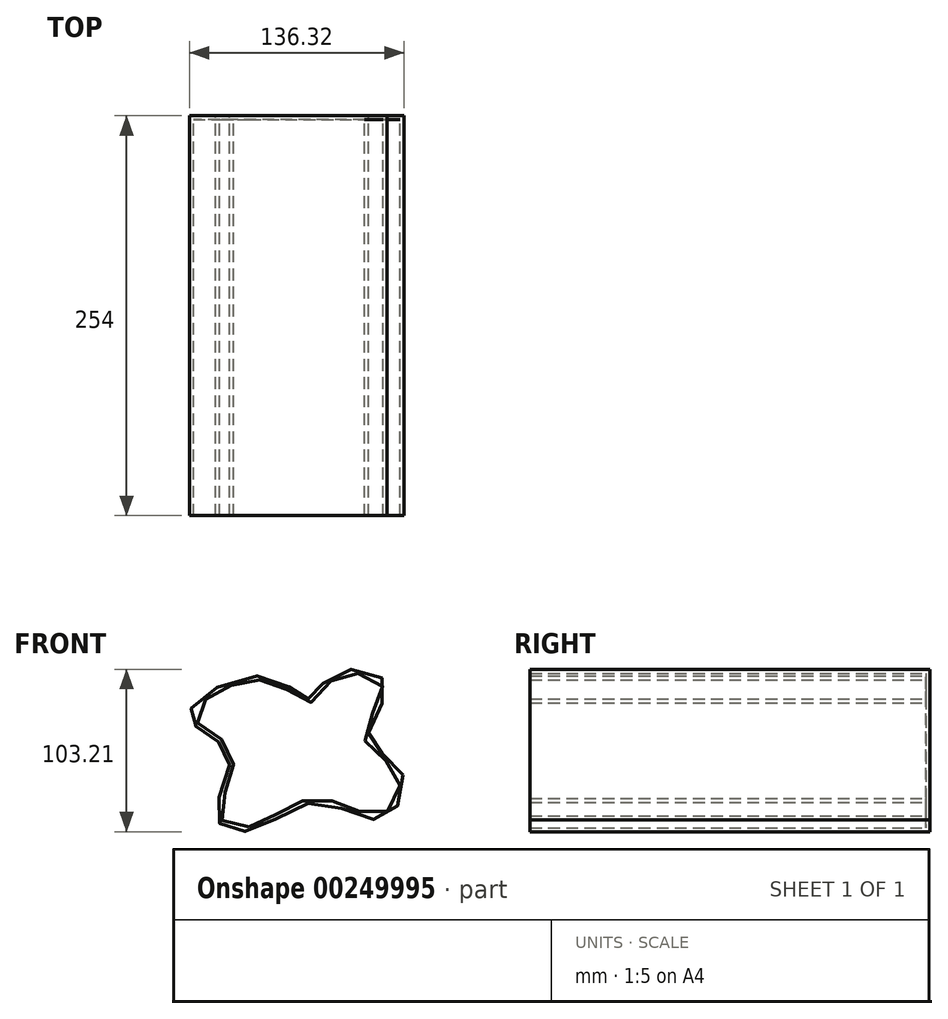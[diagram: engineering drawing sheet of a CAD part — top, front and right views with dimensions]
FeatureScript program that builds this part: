
annotation { "Feature Type Name" : "Feature", "Feature Type Description" : "" }
export const myFeature = defineFeature(function(context is Context, id is Id, definition is map)
    precondition{}
    {
        {
            var Q0;
            Q0=qCreatedBy(makeId("Front.planeOp"),FACE);
            var sketch = newSketch(context, id + "F0", { "sketchPlane" : qUnion([Q0])});
            skLineSegment(sketch, "E0.bottom", {"start": v(14.97, 40.14) * mm, "end": v(16.82, 40.14) * mm});
            skPoint(sketch, "E1.visualSharp", {"position": v(-65.1, 40.14) * mm});
            skPoint(sketch, "E2.visualSharp", {"position": v(-65.1, -45.84) * mm});
            skPoint(sketch, "E3.visualSharp", {"position": v(52.89, -45.84) * mm});
            skPoint(sketch, "E4.visualSharp", {"position": v(52.89, 40.14) * mm});
            skFitSpline(sketch, "E5", {"points": [v(-18.44, 44.2) * mm, v(-68.35, 25.22) * mm, v(-65.1, 11.93) * mm, v(-44.75, -6.5) * mm, v(-53.16, -44.2) * mm, v(-31.46, -53.43) * mm, v(11.66, -35.53) * mm, v(52.89, -45.84) * mm, v(64.82, -16.27) * mm, v(43.67, 5.7) * mm, v(55.06, 39.06) * mm, v(22.78, 46.65) * mm, v(5.42, 30.1) * mm, v(-18.44, 44.2) * mm]});
            skSolve(sketch);
        }
        {
            var Q0;
            Q0 = qSketchRegion(id + "F0", true);
            extrude(context, id + "F1", {"entities" : qUnion([Q0]), "depth" : 254 * mm});
        }
        {
            var Q0;
            Q0=makeQuery(id+"F1.opExtrude","CAP_FACE",FACE,{"disambiguationData":[OSD([sQuery(id+"F0.wireOp",EDGE,"E5")])],"isStart":false});
            shell(context, id + "F2", {"entities" : qUnion([Q0]), "thickness" : 2.54 * mm});
        }
    });
